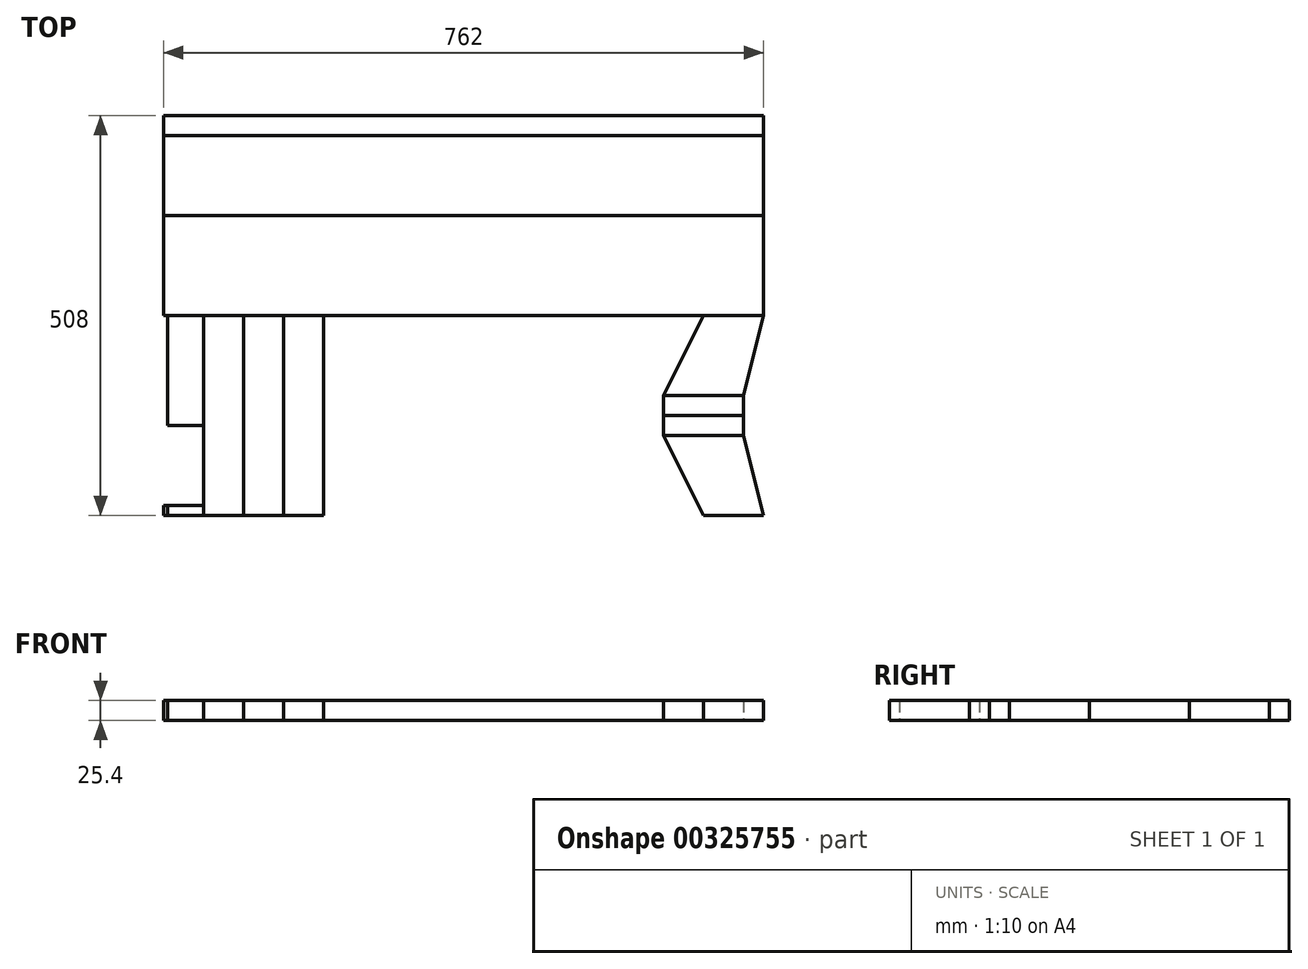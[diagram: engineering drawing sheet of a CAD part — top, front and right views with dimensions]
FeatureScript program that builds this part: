
annotation { "Feature Type Name" : "Feature", "Feature Type Description" : "" }
export const myFeature = defineFeature(function(context is Context, id is Id, definition is map)
    precondition{}
    {
        {
            var Q0;
            Q0=qCreatedBy(makeId("Top.planeOp"),FACE);
            var sketch = newSketch(context, id + "F0", { "sketchPlane" : qUnion([Q0])});
            skLineSegment(sketch, "E0.bottom", {"start": v(-381, 254) * mm, "end": v(381, 254) * mm});
            skLineSegment(sketch, "E0.left", {"start": v(-381, 254) * mm, "end": v(-381, -139.7) * mm});
            skLineSegment(sketch, "E0.right", {"start": v(381, 254) * mm, "end": v(381, -254) * mm});
            skLineSegment(sketch, "E1", {"start": v(-381, 0) * mm, "end": v(381, 0) * mm});
            skLineSegment(sketch, "E2", {"start": v(381, 254) * mm, "end": v(381, 228.6) * mm});
            skLineSegment(sketch, "E3", {"start": v(381, 228.6) * mm, "end": v(-381, 228.6) * mm});
            skLineSegment(sketch, "E4", {"start": v(-381, 228.6) * mm, "end": v(-381, 254) * mm});
            skLineSegment(sketch, "E5", {"start": v(381, 228.6) * mm, "end": v(381, 127) * mm});
            skLineSegment(sketch, "E6", {"start": v(381, 127) * mm, "end": v(-381, 127) * mm});
            skLineSegment(sketch, "E7", {"start": v(-381, 127) * mm, "end": v(-381, 228.6) * mm});
            skLineSegment(sketch, "E8", {"start": v(381, 127) * mm, "end": v(381, 0) * mm});
            skLineSegment(sketch, "E9", {"start": v(-381, -254) * mm, "end": v(-376.24, -254) * mm});
            skLineSegment(sketch, "E10", {"start": v(-381, -254) * mm, "end": v(-330.2, -254) * mm});
            skLineSegment(sketch, "E11", {"start": v(-330.2, -254) * mm, "end": v(-279.4, -254) * mm});
            skLineSegment(sketch, "E12", {"start": v(-279.4, -254) * mm, "end": v(-228.6, -254) * mm});
            skLineSegment(sketch, "E13", {"start": v(-228.6, -254) * mm, "end": v(-177.8, -254) * mm});
            skLineSegment(sketch, "E14", {"start": v(-376.24, -254) * mm, "end": v(-376.24, -241.3) * mm});
            skLineSegment(sketch, "E15", {"start": v(-330.2, -254) * mm, "end": v(-330.2, 0) * mm});
            skLineSegment(sketch, "E16", {"start": v(-279.4, -254) * mm, "end": v(-279.4, 0) * mm});
            skLineSegment(sketch, "E17", {"start": v(-228.6, -254) * mm, "end": v(-228.6, 0) * mm});
            skLineSegment(sketch, "E18", {"start": v(-177.8, -254) * mm, "end": v(-177.8, 0) * mm});
            skLineSegment(sketch, "E19", {"start": v(-381, 0) * mm, "end": v(-376.24, 0) * mm});
            skLineSegment(sketch, "E20", {"start": v(-381, -139.7) * mm, "end": v(-330.2, -139.7) * mm});
            skLineSegment(sketch, "E21", {"start": v(-381, -241.3) * mm, "end": v(-330.2, -241.3) * mm});
            skLineSegment(sketch, "E22.trimOffspring", {"start": v(-376.24, -139.7) * mm, "end": v(-376.24, 0) * mm});
            skLineSegment(sketch, "E23.trimOffspring", {"start": v(-381, -241.3) * mm, "end": v(-381, -254) * mm});
            skLineSegment(sketch, "E24", {"start": v(381, 0) * mm, "end": v(381, -254) * mm});
            skLineSegment(sketch, "E25", {"start": v(254, -127) * mm, "end": v(254, -152.4) * mm});
            skLineSegment(sketch, "E26", {"start": v(254, -127) * mm, "end": v(254, -101.6) * mm});
            skLineSegment(sketch, "E27.bottom", {"start": v(254, -101.6) * mm, "end": v(355.6, -101.6) * mm});
            skLineSegment(sketch, "E27.top", {"start": v(254, -127) * mm, "end": v(355.6, -127) * mm});
            skLineSegment(sketch, "E27.right", {"start": v(355.6, -101.6) * mm, "end": v(355.6, -127) * mm});
            skLineSegment(sketch, "E28.bottom", {"start": v(355.6, -127) * mm, "end": v(254, -127) * mm});
            skLineSegment(sketch, "E28.top", {"start": v(355.6, -152.4) * mm, "end": v(254, -152.4) * mm});
            skLineSegment(sketch, "E28.left", {"start": v(355.6, -127) * mm, "end": v(355.6, -152.4) * mm});
            skLineSegment(sketch, "E29", {"start": v(381, 0) * mm, "end": v(304.8, 0) * mm});
            skLineSegment(sketch, "E30", {"start": v(381, -254) * mm, "end": v(304.8, -254) * mm});
            skLineSegment(sketch, "E31", {"start": v(381, -254) * mm, "end": v(355.6, -152.4) * mm});
            skLineSegment(sketch, "E32", {"start": v(355.6, -101.6) * mm, "end": v(381, 0) * mm});
            skLineSegment(sketch, "E33", {"start": v(254, -101.6) * mm, "end": v(304.8, 0) * mm});
            skLineSegment(sketch, "E34", {"start": v(304.8, -254) * mm, "end": v(254, -152.4) * mm});
            skLineSegment(sketch, "E35", {"start": v(381, -254) * mm, "end": v(-381, -254) * mm});
            skSolve(sketch);
        }
        {
            var Q0;
            Q0=makeQuery(id+"F0.imprint","IMPRINT",FACE,{"disambiguationData":[TD([[makeQuery(id+"F0.imprint","IMPRINT",EDGE,{"derivedFrom":sQuery(id+"F0.wireOp",EDGE,"E28.top")}),1.0]])]});
            var Q1;
            {var subQ0=sQuery(id+"F0.wireOp",EDGE,"E0.bottom");Q1=makeQuery(id+"F0.imprint","IMPRINT",FACE,{"disambiguationData":[TD([[makeQuery(id+"F0.imprint","IMPRINT",EDGE,{"derivedFrom":subQ0}),-1.0]])]});}
            var Q2;
            {var subQ4=sQuery(id+"F0.wireOp",EDGE,"E6");Q2=makeQuery(id+"F0.imprint","IMPRINT",FACE,{"disambiguationData":[TD([[makeQuery(id+"F0.imprint","IMPRINT",EDGE,{"derivedFrom":subQ4}),1.0]])]});}
            var Q3;
            Q3=makeQuery(id+"F0.imprint","IMPRINT",FACE,{"disambiguationData":[TD([[makeQuery(id+"F0.imprint","IMPRINT",EDGE,{"derivedFrom":sQuery(id+"F0.wireOp",EDGE,"E26")}),-1.0]])]});
            var Q4;
            {var subQ0=sQuery(id+"F0.wireOp",EDGE,"E14");Q4=makeQuery(id+"F0.imprint","IMPRINT",FACE,{"disambiguationData":[TD([[makeQuery(id+"F0.imprint","IMPRINT",EDGE,{"derivedFrom":subQ0}),-1.0]])]});}
            extrude(context, id + "F1", {"entities" : qUnion([Q0, Q1, Q2, Q3, Q4]), "depth" : 25.4 * mm});
        }
        {
            var Q0;
            Q0=makeQuery(id+"F0.imprint","IMPRINT",FACE,{"disambiguationData":[TD([[makeQuery(id+"F0.imprint","IMPRINT",EDGE,{"derivedFrom":sQuery(id+"F0.wireOp",EDGE,"E27.bottom")}),1.0]])]});
            var Q1;
            {var subQ0=sQuery(id+"F0.wireOp",EDGE,"E3");Q1=makeQuery(id+"F0.imprint","IMPRINT",FACE,{"disambiguationData":[TD([[makeQuery(id+"F0.imprint","IMPRINT",EDGE,{"derivedFrom":subQ0}),1.0]])]});}
            var Q2;
            {var subQ0=sQuery(id+"F0.wireOp",EDGE,"E17");Q2=makeQuery(id+"F0.imprint","IMPRINT",FACE,{"disambiguationData":[TD([[makeQuery(id+"F0.imprint","IMPRINT",EDGE,{"derivedFrom":subQ0}),-1.0]])]});}
            var Q3;
            {var subQ5=sQuery(id+"F0.wireOp",EDGE,"E16");Q3=makeQuery(id+"F0.imprint","IMPRINT",FACE,{"disambiguationData":[TD([[makeQuery(id+"F0.imprint","IMPRINT",EDGE,{"derivedFrom":subQ5}),1.0]])]});}
            var Q4;
            {var subQ0=sQuery(id+"F0.wireOp",EDGE,"E19");Q4=makeQuery(id+"F0.imprint","IMPRINT",FACE,{"disambiguationData":[TD([[makeQuery(id+"F0.imprint","IMPRINT",EDGE,{"derivedFrom":subQ0}),-1.0]])]});}
            var Q5;
            {var subQ0=sQuery(id+"F0.wireOp",EDGE,"E14");Q5=makeQuery(id+"F0.imprint","IMPRINT",FACE,{"disambiguationData":[TD([[makeQuery(id+"F0.imprint","IMPRINT",EDGE,{"derivedFrom":subQ0}),1.0]])]});}
            var Q6;
            Q6=makeQuery(id+"F0.imprint","IMPRINT",FACE,{"disambiguationData":[TD([[makeQuery(id+"F0.imprint","IMPRINT",EDGE,{"derivedFrom":sQuery(id+"F0.wireOp",EDGE,"E25")}),1.0]])]});
            extrude(context, id + "F2", {"entities" : qUnion([Q0, Q1, Q2, Q3, Q4, Q5, Q6]), "depth" : 25.4 * mm});
        }
        {
            var Q0;
            {var subQ0=sQuery(id+"F0.wireOp",EDGE,"E16");Q0=makeQuery(id+"F0.imprint","IMPRINT",FACE,{"disambiguationData":[TD([[makeQuery(id+"F0.imprint","IMPRINT",EDGE,{"derivedFrom":subQ0}),-1.0]])]});}
            var Q1;
            {var subQ0=sQuery(id+"F0.wireOp",EDGE,"E22.trimOffspring");Q1=makeQuery(id+"F0.imprint","IMPRINT",FACE,{"disambiguationData":[TD([[makeQuery(id+"F0.imprint","IMPRINT",EDGE,{"derivedFrom":subQ0}),-1.0]])]});}
            extrude(context, id + "F3", {"entities" : qUnion([Q0, Q1]), "depth" : 25.4 * mm});
        }
    });
